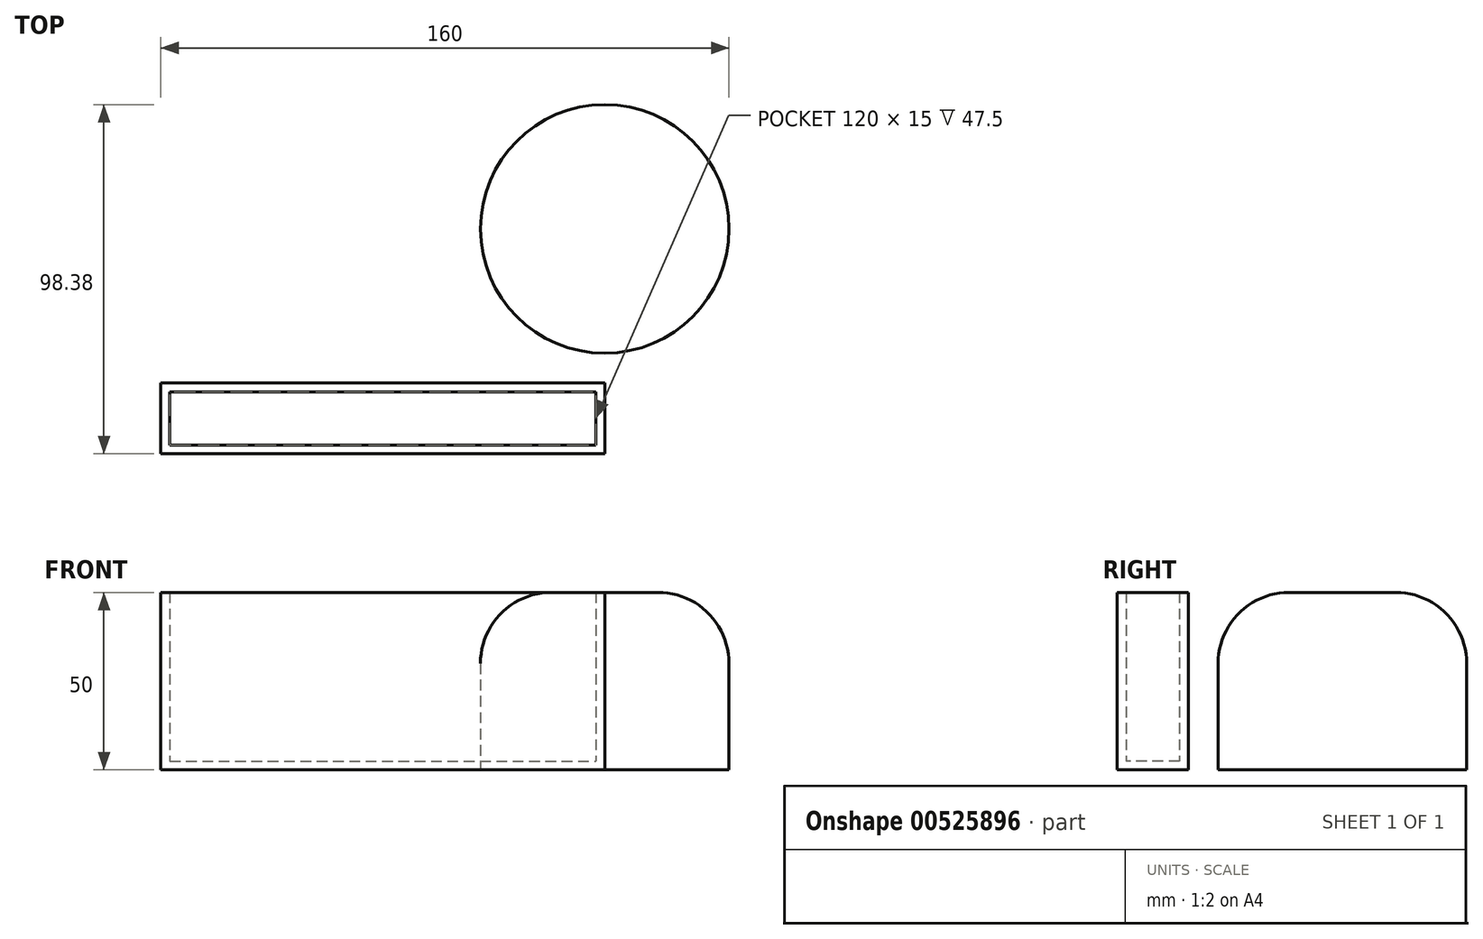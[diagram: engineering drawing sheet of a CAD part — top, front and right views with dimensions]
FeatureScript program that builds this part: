
annotation { "Feature Type Name" : "Feature", "Feature Type Description" : "" }
export const myFeature = defineFeature(function(context is Context, id is Id, definition is map)
    precondition{}
    {
        {
            var Q0;
            Q0=qCreatedBy(makeId("Top.planeOp"),FACE);
            var sketch = newSketch(context, id + "F0", { "sketchPlane" : qUnion([Q0])});
            skLineSegment(sketch, "E0.bottom", {"start": v(-125, 20) * mm, "end": v(0, 20) * mm});
            skLineSegment(sketch, "E0.top", {"start": v(-125, 0) * mm, "end": v(0, 0) * mm});
            skLineSegment(sketch, "E0.left", {"start": v(-125, 20) * mm, "end": v(-125, 0) * mm});
            skLineSegment(sketch, "E0.right", {"start": v(0, 20) * mm, "end": v(0, 0) * mm});
            skCircle(sketch, "E1", {"center": v(0, 63.38) * mm, "radius": 35 * mm});
            skSolve(sketch);
        }
        {
            var Q0;
            {var subQ0=sQuery(id+"F0.wireOp",EDGE,"E0.right");var subQ1=sQuery(id+"F0.wireOp",EDGE,"E0.bottom");var subQ2=makeQuery(id+"F0.imprint","INTERSECT",VERTEX,{"derivedFrom":[subQ1,subQ0]});Q0=makeQuery(id+"F0.imprint","IMPRINT",FACE,{"disambiguationData":[TD([[makeQuery(id+"F0.imprint","IMPRINT",EDGE,{"disambiguationData":[TD([[subQ2,1.0]])],"derivedFrom":subQ1}),1.0]])]});}
            var Q1;
            {var subQ1=sQuery(id+"F0.wireOp",EDGE,"E0.top");Q1=makeQuery(id+"F0.imprint","IMPRINT",FACE,{"disambiguationData":[TD([[makeQuery(id+"F0.imprint","IMPRINT",EDGE,{"derivedFrom":subQ1}),1.0]])]});}
            var Q2;
            Q2=makeQuery(id+"F0.imprint","IMPRINT",FACE,{"disambiguationData":[TD([[makeQuery(id+"F0.imprint","IMPRINT",EDGE,{"derivedFrom":sQuery(id+"F0.wireOp",EDGE,"E1")}),1.0]])]});
            extrude(context, id + "F1", {"entities" : qUnion([Q0, Q1, Q2]), "depth" : 50 * mm, "offsetDistance" : 25 * mm});
        }
        {
            var Q0;
            {var subQ0=sQuery(id+"F0.wireOp",EDGE,"E1");Q0=makeQuery(id+"F1.opExtrude","CAP_EDGE",EDGE,{"disambiguationData":[OSD([subQ0]),TDD([makeQuery(id+"F0.imprint","IMPRINT",EDGE,{"disambiguationData":[TD([[makeQuery(id+"F0.imprint","INTERSECT",VERTEX,{"derivedFrom":[sQuery(id+"F0.wireOp",EDGE,"E0.bottom"),subQ0]}),1.0]])],"derivedFrom":subQ0})])],"isStart":false});}
            fillet(context, id + "F2", {"entities" : qUnion([Q0]), "radius" : 20 * mm, "tangentPropagation" : true, "allowEdgeOverflow" : false});
        }
        {
            var Q0;
            Q0=makeQuery(id+"F1.opExtrude","CAP_FACE",FACE,{"disambiguationData":[OSD([sQuery(id+"F0.wireOp",EDGE,"E0.bottom"),sQuery(id+"F0.wireOp",EDGE,"E0.top"),sQuery(id+"F0.wireOp",EDGE,"E0.left"),sQuery(id+"F0.wireOp",EDGE,"E0.right"),sQuery(id+"F0.wireOp",EDGE,"E1")])],"isStart":false});
            shell(context, id + "F3", {"entities" : qUnion([Q0]), "thickness" : 2.5 * mm});
        }
    });
